# Revit family: Falcon-Tufgrain-8789-Aluminum Side Chair
name_source: partatom
category: Furniture
units: mm (PartAtom-declared; Revit-internal decimal feet)

## family parameters
Always vertical = Yes
Cut with Voids When Loaded = No
OmniClass Number = 23.40.20.00
OmniClass Title = General Furniture and Specialties
Room Calculation Point = No
Shared = No
Work Plane-Based = No

## types (1)
- Falcon-Tufgrain-8789-Aluminum Side Chair
    COM Yardage = 1 yds
    Default Elevation = 0"
    Depth = 22 1/2"
    Description = Aluminum Side Chair
    Height = 33 1/2"
    Manufacturer = Falcon
    Manufacturer Fax = 866-319-9371
    Model = 8789
    Product Line = Tufgrain
    Revit Object Download Link = https://www.falconproducts.com
    Seat Height = 18 1/2"
    Type Image = 8789 Front Angle.jpg
    URL = https://www.falconproducts.com
    Weight Capacity = 350 lbs.
    Width = 21 1/2"

## geometry (parser evidence)
native form markers: Sweep x3
no freeform markers — native parametric forms only
